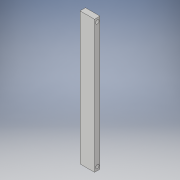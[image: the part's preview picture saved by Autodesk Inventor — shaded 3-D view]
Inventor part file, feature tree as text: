
AUTODESK INVENTOR PART (.ipt)
format: ipt  version: 2017 (Build 210142000, 142)  size: 98,304 bytes
history: native  units: in
note: dims shown in document units (in); Inventor stores cm internally (conversion verified against a paired STEP export)
features: extrude x1, sketch x1
ambient origin geometry x8: Origin, YZ Plane, XZ Plane, XY Plane, X Axis, Y Axis, Z Axis, Center Point
bodies: Solid1 (feature_tree)
feature tree (2):
  extrude  "Extrusion1"  Depth=0.75in
  sketch  "Sketch1"  dims[d0=18.25in d1=0.75in d2=0.5in d3=0.5in d4=0.5in d5=0.5in d6=2.0in d7=0.0in]
